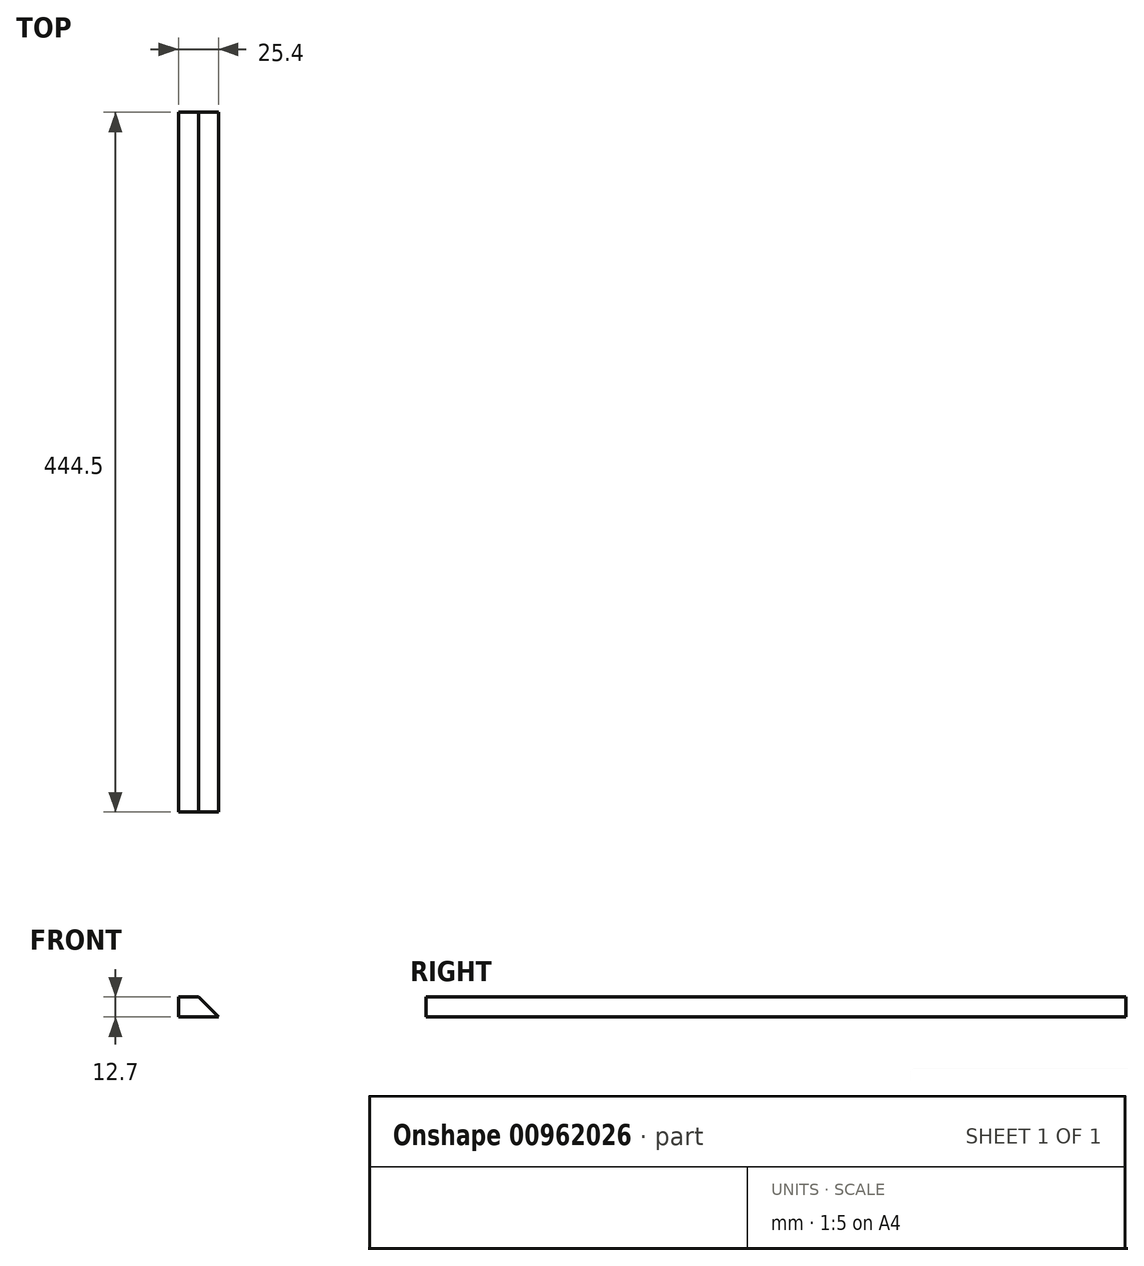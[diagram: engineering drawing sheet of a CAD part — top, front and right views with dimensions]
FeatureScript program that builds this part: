
annotation { "Feature Type Name" : "Feature", "Feature Type Description" : "" }
export const myFeature = defineFeature(function(context is Context, id is Id, definition is map)
    precondition{}
    {
        {
            var Q0;
            Q0=qCreatedBy(makeId("Front.planeOp"),FACE);
            var sketch = newSketch(context, id + "F0", { "sketchPlane" : qUnion([Q0])});
            skLineSegment(sketch, "E0", {"start": v(0, 0) * mm, "end": v(-12.7, 0) * mm});
            skLineSegment(sketch, "E1", {"start": v(-12.7, 0) * mm, "end": v(-12.7, 12.7) * mm});
            skLineSegment(sketch, "E2", {"start": v(-12.7, 12.7) * mm, "end": v(0, 12.7) * mm});
            skLineSegment(sketch, "E3", {"start": v(0, 12.7) * mm, "end": v(12.7, 0) * mm});
            skLineSegment(sketch, "E4", {"start": v(12.7, 0) * mm, "end": v(0, 0) * mm});
            skSolve(sketch);
        }
        {
            var Q0;
            Q0 = qSketchRegion(id + "F0", true);
            extrude(context, id + "F1", {"entities" : qUnion([Q0]), "endBound" : BoundingType.SYMMETRIC, "depth" : 444.5 * mm, "offsetDistance" : 25.4 * mm});
        }
    });
